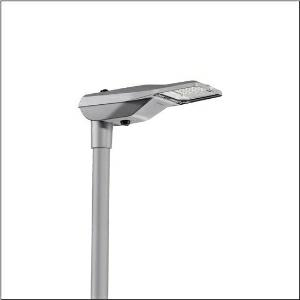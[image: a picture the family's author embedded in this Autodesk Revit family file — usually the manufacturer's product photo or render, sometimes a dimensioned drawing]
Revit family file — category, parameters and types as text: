
# Revit family: streetlight_sl_21_iq_micro___p0_8ab_5xe1r31y08db_c2fe
name_source: partatom
category: Lighting Fixtures
units: mm (PartAtom-declared; Revit-internal decimal feet)

## family parameters
Cut with Voids When Loaded = No
Host = Face
Light Source = No
Part Type = Normal
Room Calculation Point = No
Round Connector Dimension = Use Diameter
Shared = No

## types (1)
- --- (1 x LED, 4550 lm, 39.1 W, 3000K)
    Apparent Load = 39 VA
    CIE Flux Codes = 36 71 98 100 100
    Color Rendering = 70
    Color Temperature = 3000K
    Default Elevation = 1800 mm
    Description = Streetlight SL 21 iQ micro, mast luminaire, primary light control with lens, of PMMA, primary optical cover: cover, of toughened safety glass, transparent, light distribution: P0.8aB, light emission: direct distribution, primary light characteristic: asymmetric, installation type: post-top, side-entry, LED, High Power LED, rated luminous flux: 4.550lm, luminous efficacy: 116lm/W, light colour: 730, colour temperature: 3000K, control gear: iQ-Street Remote, D4i with power reduction, control: pre-setting: logarithmic dimming characteristic, Street-Remote, Auto-Match, Temp-Guard, Lumen-Switch, Night-Set, Smart-Wire, Light-Fading, Desk-Remote (wireless, voltage-free reading and setting of iQ features in the workshop via application-optimized NFC function/RFID function), optimised constant luminous flux control (CLO 2.0), mains connection: 220..240V, AC, 50/60Hz, start of lifetime: 39W, end of service life: 41W, reduction: 17W, luminaire housing, of diecast aluminium, powder-coated, Siteco® metallic grey (DB 702S), corrosivity category C5 mid according to DIN EN ISO 12944, please order mast flange separately, inclination adjustable: 0°, 5°, 10°, 15°, sealing non-destructively replaceable, multi-level sealing system, length: 528mm, width: 235mm, height: 110mm, mast flange for spigot size: 42mm (side-entry): 5XC10008XM4, 60/48mm (side-entry/post-top): 5XC10108XM2, 76/60mm (side-entry/post-top): 5XC10108XM1, mounting height: 4..8m, Smart Interface below and above, protection rating (complete): IP66, insulation class (complete): insulation class II (safety insulation), certification: CE, ENEC, ENEC+, VDE, impact resistance: IK09, permissible operating ambient temperature for outdoor applications: -40..+50°C, standard-compliant lighting for roads and squares, packaging unit: 1 piece

Light Distribution: P0.8aB
    Height = 110 mm
    Lamp = 1 x LED
    Lamp Light Flux = 4550 lm
    Lamp Power = 39.1 W
    Lamp count = 1
    Length = 528 mm
    Luminous efficacy = 116 lm/W
    Manufacturer = Siteco
    ModVariant = No
    Model = 5XE1R31Y08DB
    Number of Poles = 1
    OnlyDefault = Yes
    Power Factor = 1
    Product Name = Streetlight SL 21 iQ micro | P0.8aB
    Product group = mast luminaire | pylon top
    ProductGroupID = 6100
    Protection Class = Protection class II
    Protection Degree = IP 66
    RLX_Detail_Level = 1
    RLX_Emergency_Light_Flux = 0 lm
    RLX_Emergency_Type = 0
    RLX_Emergency_Type_DB = No
    RlxData = <blob elided: 99005 chars, md5=af79c3b4>
    Socket = socket
    Standby Power = 0 W
    System Light Flux = 4550 lm
    System Power = 39 W
    Type Comments = factory setting: luminous flux: 100 % | dim-lin: 254 | 765 mA
    Type Image = l_1007239.jpg
    URL = http://relux.com
    VarID = @adj_072732
    Voltage = 0 V
    Weight = 0.00 kg
    Width = 235 mm

## geometry (parser evidence)
native form markers: Blend x4, Sweep x9
no freeform markers — native parametric forms only
